# Revit family: tomas no bloqueados salientes 480_500V
name_source: partatom
category: Installations électriques
revit_build: Autodesk Revit 2018 (Build: 20170223_1515(x64)
units: mm (PartAtom-declared; Revit-internal decimal feet)

## family parameters
Conserver l'orientation des annotations = Non
Cote de connecteur circulaire = Utiliser le diamètre
Couper avec des vides une fois chargée = Non
Hôte = Face
Partagée = Non
Point de calcul de pièce = Non
Type d'élément = Normal

## types (8) — shared parameters
Elévation par défaut = 1000 mm  [stored 3.28084 ft]
Estándar CEI o NFC = CEI
Fabricant = Legrand
Familia produce = 0854-P17 TEMPRA PRO
Temperatura maxima de uso = 40
Temperatura minima de instalación = -5
Temperatura minima de uso = -25
Tension V = 500 V  50/60 Hz negro
Toma estándar internacional para montaje empotrado o montaje en superficie con accesorio permite la conexión de dispositivos de alimentación = Toma estándar internacional para montaje empotrado o montaje en superficie con accesorio permite la conexión de dispositivos de alimentación
color característico = negro
materia de la caja = plástico
posición de la tierra h = 7
resistencia a los choques IK = 9
tipo de conexión = conexión por tonillo
tipo de enclavamiento = x

## per-type parameters (varying)
| type | Description | Diámetro de entrada del cable | Modèle | altura mm | ancho mm | clase de protección IP | distancia de fijación horizontal mm | distancia de fijación vertical mm | intensidad A | numero de polos | profundidad mm | sin halogeno |
| IDS_LG_555162 | IDS_DESCRIPTION_LG_555162 | M20/M25 | LG-555162 | 131 mm  [stored 0.42979 ft] | 93 mm | IP44 | 70 mm | 0 mm  [stored 0 ft] | 16 A | 4 | 133 mm  [stored 0.436352 ft] | Oui |
| IDS_LG_555163 | IDS_DESCRIPTION_LG_555163 | M20/M25 | LG-555163 | 131 mm  [stored 0.42979 ft] | 93 mm | IP44 | 70 mm | 0 mm  [stored 0 ft] | 16 A | 5 | 139 mm | Oui |
| IDS_LG_555262 | IDS_DESCRIPTION_LG_555262 | M25/M32 | LG-555262 | 156 mm  [stored 0.511811 ft] | 113 mm | IP44 | 90 mm | 0 mm  [stored 0 ft] | 32 A | 4 | 155 mm | Oui |
| IDS_LG_555263 | IDS_DESCRIPTION_LG_555263 | M25/M32 | LG-555263 | 156 mm  [stored 0.511811 ft] | 113 mm | IP44 | 90 mm | 0 mm  [stored 0 ft] | 32 A | 5 | 161 mm | Oui |
| IDS_LG_555362 | IDS_DESCRIPTION_LG_555362 | M20/M25 | LG-555362 | 138 mm  [stored 0.452756 ft] | 93 mm |  | 70 mm | 0 mm  [stored 0 ft] | 16 A | 4 | 134 mm  [stored 0.439633 ft] | Non |
| IDS_LG_555462 | IDS_DESCRIPTION_LG_555462 | M25/M32 | LG-555462 | 163 mm  [stored 0.534777 ft] | 113 mm |  | 90 mm | 0 mm  [stored 0 ft] | 32 A | 4 | 156 mm  [stored 0.511811 ft] | Non |
| IDS_LG_555463 | IDS_DESCRIPTION_LG_555463 | M25/M32 | LG-555463 | 163 mm  [stored 0.534777 ft] | 113 mm |  | 90 mm | 0 mm  [stored 0 ft] | 32 A | 5 | 162 mm | Non |
| IDS_LG_555562 | IDS_DESCRIPTION_LG_555562 | M32 | LG-555562 | 270 mm  [stored 0.885827 ft] | 130 mm |  | 119 mm | 156 mm  [stored 0.511811 ft] | 63 A | 4 | 190 mm | Non |

note: [stored X ft] marks values corroborated as IEEE doubles in the binary element streams (Revit-internal decimal feet)
